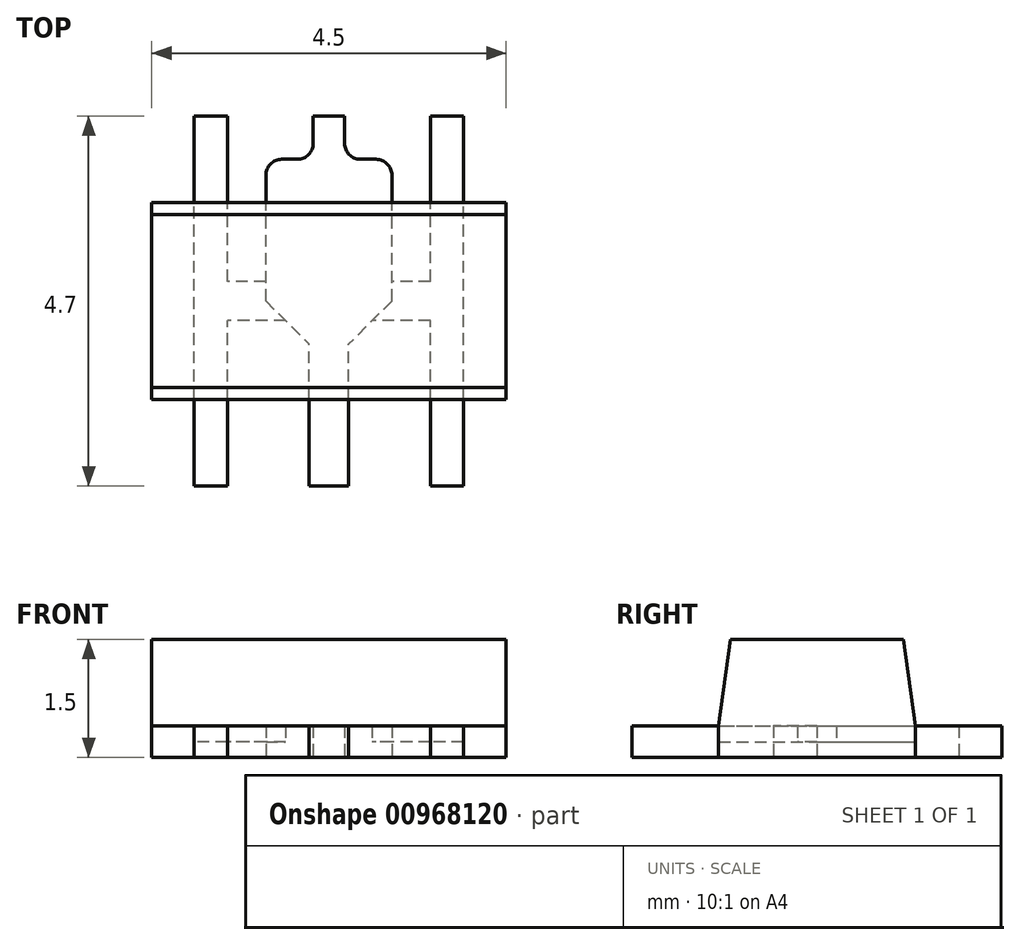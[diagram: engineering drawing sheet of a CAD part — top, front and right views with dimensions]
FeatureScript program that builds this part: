
annotation { "Feature Type Name" : "Feature", "Feature Type Description" : "" }
export const myFeature = defineFeature(function(context is Context, id is Id, definition is map)
    precondition{}
    {
        {
            assignVariable(context, id + "F0", {"name" : "A", "anyValue" : 1.5});
        }
        {
            assignVariable(context, id + "F1", {"name" : "E", "anyValue" : 2.5});
        }
        {
            assignVariable(context, id + "F2", {"name" : "E1", "anyValue" : 2.2});
        }
        {
            assignVariable(context, id + "F3", {"name" : "c", "anyValue" : 0.4});
        }
        {
            var Q0;
            Q0=qCreatedBy(makeId("Top.planeOp"),FACE);
            var sketch = newSketch(context, id + "F4", { "sketchPlane" : qUnion([Q0])});
            skLineSegment(sketch, "E0.bottom", {"start": v(2.25, -1.25) * mm, "end": v(-2.25, -1.25) * mm});
            skLineSegment(sketch, "E0.top", {"start": v(2.25, 1.25) * mm, "end": v(-2.25, 1.25) * mm});
            skLineSegment(sketch, "E0.left", {"start": v(2.25, -1.25) * mm, "end": v(2.25, 1.25) * mm});
            skLineSegment(sketch, "E0.right", {"start": v(-2.25, -1.25) * mm, "end": v(-2.25, 1.25) * mm});
            skPoint(sketch, "E0.middle", {"position": v(0, 0) * mm});
            skLineSegment(sketch, "E1.bottom", {"start": v(0.25, -2.35) * mm, "end": v(-0.25, -2.35) * mm});
            skLineSegment(sketch, "E1.left", {"start": v(0.25, -2.35) * mm, "end": v(0.25, -0.55) * mm});
            skLineSegment(sketch, "E1.right", {"start": v(-0.25, -2.35) * mm, "end": v(-0.25, -0.55) * mm});
            skPoint(sketch, "E1.middle", {"position": v(0, -1.17) * mm});
            skLineSegment(sketch, "E2.bottom", {"start": v(1.71, -2.35) * mm, "end": v(1.29, -2.35) * mm});
            skLineSegment(sketch, "E2.top", {"start": v(1.71, 2.35) * mm, "end": v(1.29, 2.35) * mm});
            skLineSegment(sketch, "E2.left", {"start": v(1.29, -2.35) * mm, "end": v(1.29, 2.35) * mm});
            skLineSegment(sketch, "E2.right", {"start": v(1.71, -2.35) * mm, "end": v(1.71, 2.35) * mm});
            skPoint(sketch, "E2.middle", {"position": v(1.5, 0) * mm});
            skLineSegment(sketch, "E3.top", {"start": v(0.2, 2.35) * mm, "end": v(-0.2, 2.35) * mm});
            skLineSegment(sketch, "E3.left", {"start": v(-0.2, 1.8) * mm, "end": v(-0.2, 2.35) * mm});
            skLineSegment(sketch, "E3.right", {"start": v(0.2, 1.8) * mm, "end": v(0.2, 2.35) * mm});
            skPoint(sketch, "E3.middle", {"position": v(0, 1.17) * mm});
            skLineSegment(sketch, "E4.bottom", {"start": v(-1.29, -2.35) * mm, "end": v(-1.7, -2.35) * mm});
            skLineSegment(sketch, "E4.top", {"start": v(-1.29, 2.35) * mm, "end": v(-1.7, 2.35) * mm});
            skLineSegment(sketch, "E4.left", {"start": v(-1.29, -2.35) * mm, "end": v(-1.29, 2.35) * mm});
            skLineSegment(sketch, "E4.right", {"start": v(-1.7, -2.35) * mm, "end": v(-1.7, 2.35) * mm});
            skPoint(sketch, "E4.middle", {"position": v(-1.5, 0) * mm});
            skLineSegment(sketch, "E5.top", {"start": v(0.8, 1.8) * mm, "end": v(0.2, 1.8) * mm});
            skLineSegment(sketch, "E5.left", {"start": v(0.8, 0) * mm, "end": v(0.8, 1.8) * mm});
            skLineSegment(sketch, "E5.right", {"start": v(-0.8, 0) * mm, "end": v(-0.8, 1.8) * mm});
            skPoint(sketch, "E5.middle", {"position": v(0, 0.9) * mm});
            skLineSegment(sketch, "E6", {"start": v(-1.29, -2.35) * mm, "end": v(-0.25, -2.35) * mm, "construction": true});
            skLineSegment(sketch, "E7", {"start": v(-0.2, 2.35) * mm, "end": v(0.2, 2.35) * mm, "construction": true});
            skLineSegment(sketch, "E8", {"start": v(-1.29, 2.35) * mm, "end": v(-0.2, 2.35) * mm, "construction": true});
            skLineSegment(sketch, "E9", {"start": v(0.2, 2.35) * mm, "end": v(1.29, 2.35) * mm, "construction": true});
            skLineSegment(sketch, "E10", {"start": v(0.25, -2.35) * mm, "end": v(1.29, -2.35) * mm, "construction": true});
            skPoint(sketch, "E11.orphan", {"position": v(-0.2, 0) * mm});
            skPoint(sketch, "E12.orphan", {"position": v(0.2, 0) * mm});
            skLineSegment(sketch, "E13.trimOffspring", {"start": v(-0.2, 1.8) * mm, "end": v(-0.8, 1.8) * mm});
            skLineSegment(sketch, "E14.bottom", {"start": v(1.71, -0.25) * mm, "end": v(-1.71, -0.25) * mm});
            skLineSegment(sketch, "E14.top", {"start": v(1.71, 0.25) * mm, "end": v(-1.71, 0.25) * mm});
            skLineSegment(sketch, "E14.left", {"start": v(1.71, -0.25) * mm, "end": v(1.71, 0.25) * mm});
            skLineSegment(sketch, "E14.right", {"start": v(-1.71, -0.25) * mm, "end": v(-1.71, 0.25) * mm});
            skLineSegment(sketch, "E15", {"start": v(-0.8, 0) * mm, "end": v(-0.25, -0.55) * mm});
            skLineSegment(sketch, "E16", {"start": v(0.8, 0) * mm, "end": v(0.25, -0.55) * mm});
            skPoint(sketch, "E17.orphan", {"position": v(-0.25, 0) * mm});
            skPoint(sketch, "E5.bottom.end.orphan", {"position": v(0.25, 0) * mm});
            skSolve(sketch);
        }
        {
            var Q0;
            {var subQ0=sQuery(id+"F4.wireOp",EDGE,"E5.left");var subQ1=sQuery(id+"F4.wireOp",EDGE,"E0.top");var subQ2=makeQuery(id+"F4.imprint","INTERSECT",VERTEX,{"derivedFrom":[subQ1,subQ0]});Q0=makeQuery(id+"F4.imprint","IMPRINT",FACE,{"disambiguationData":[TD([[makeQuery(id+"F4.imprint","IMPRINT",EDGE,{"disambiguationData":[TD([[subQ2,-1.0]])],"derivedFrom":subQ1}),1.0]])]});}
            var Q1;
            {var subQ0=sQuery(id+"F4.wireOp",EDGE,"E14.top");var subQ1=sQuery(id+"F4.wireOp",EDGE,"E4.left");var subQ2=makeQuery(id+"F4.imprint","INTERSECT",VERTEX,{"derivedFrom":[subQ1,subQ0]});Q1=makeQuery(id+"F4.imprint","IMPRINT",FACE,{"disambiguationData":[TD([[makeQuery(id+"F4.imprint","IMPRINT",EDGE,{"disambiguationData":[TD([[subQ2,1.0]])],"derivedFrom":subQ1}),-1.0]])]});}
            var Q2;
            {var subQ0=sQuery(id+"F4.wireOp",EDGE,"E14.top");var subQ5=sQuery(id+"F4.wireOp",EDGE,"E5.left");var subQ6=makeQuery(id+"F4.imprint","INTERSECT",VERTEX,{"derivedFrom":[subQ5,subQ0]});Q2=makeQuery(id+"F4.imprint","IMPRINT",FACE,{"disambiguationData":[TD([[makeQuery(id+"F4.imprint","IMPRINT",EDGE,{"disambiguationData":[TD([[subQ6,1.0]])],"derivedFrom":subQ5}),1.0]])]});}
            var Q3;
            {var subQ7=sQuery(id+"F4.wireOp",EDGE,"E0.bottom");var subQ9=sQuery(id+"F4.wireOp",EDGE,"E1.left");var subQ11=makeQuery(id+"F4.imprint","INTERSECT",VERTEX,{"derivedFrom":[subQ7,subQ9]});Q3=makeQuery(id+"F4.imprint","IMPRINT",FACE,{"disambiguationData":[TD([[makeQuery(id+"F4.imprint","IMPRINT",EDGE,{"disambiguationData":[TD([[subQ11,-1.0]])],"derivedFrom":subQ7}),-1.0]])]});}
            var Q4;
            {var subQ0=sQuery(id+"F4.wireOp",EDGE,"E14.top");var subQ1=sQuery(id+"F4.wireOp",EDGE,"E4.left");var subQ2=makeQuery(id+"F4.imprint","INTERSECT",VERTEX,{"derivedFrom":[subQ1,subQ0]});Q4=makeQuery(id+"F4.imprint","IMPRINT",FACE,{"disambiguationData":[TD([[makeQuery(id+"F4.imprint","IMPRINT",EDGE,{"disambiguationData":[TD([[subQ2,1.0]])],"derivedFrom":subQ1}),1.0]])]});}
            var Q5;
            {var subQ0=sQuery(id+"F4.wireOp",EDGE,"E4.right");var subQ1=sQuery(id+"F4.wireOp",EDGE,"E0.top");var subQ2=makeQuery(id+"F4.imprint","INTERSECT",VERTEX,{"derivedFrom":[subQ1,subQ0]});Q5=makeQuery(id+"F4.imprint","IMPRINT",FACE,{"disambiguationData":[TD([[makeQuery(id+"F4.imprint","IMPRINT",EDGE,{"disambiguationData":[TD([[subQ2,1.0]])],"derivedFrom":subQ1}),1.0]])]});}
            var Q6;
            {var subQ0=sQuery(id+"F4.wireOp",EDGE,"E4.left");var subQ1=sQuery(id+"F4.wireOp",EDGE,"E0.bottom");var subQ2=makeQuery(id+"F4.imprint","INTERSECT",VERTEX,{"derivedFrom":[subQ1,subQ0]});Q6=makeQuery(id+"F4.imprint","IMPRINT",FACE,{"disambiguationData":[TD([[makeQuery(id+"F4.imprint","IMPRINT",EDGE,{"disambiguationData":[TD([[subQ2,-1.0]])],"derivedFrom":subQ1}),-1.0]])]});}
            var Q7;
            {var subQ5=sQuery(id+"F4.wireOp",EDGE,"E4.bottom");Q7=makeQuery(id+"F4.imprint","IMPRINT",FACE,{"disambiguationData":[TD([[makeQuery(id+"F4.imprint","IMPRINT",EDGE,{"derivedFrom":subQ5}),-1.0]])]});}
            var Q8;
            {var subQ5=sQuery(id+"F4.wireOp",EDGE,"E1.bottom");Q8=makeQuery(id+"F4.imprint","IMPRINT",FACE,{"disambiguationData":[TD([[makeQuery(id+"F4.imprint","IMPRINT",EDGE,{"derivedFrom":subQ5}),-1.0]])]});}
            var Q9;
            {var subQ0=sQuery(id+"F4.wireOp",EDGE,"E14.top");var subQ5=sQuery(id+"F4.wireOp",EDGE,"E2.left");var subQ6=makeQuery(id+"F4.imprint","INTERSECT",VERTEX,{"derivedFrom":[subQ5,subQ0]});Q9=makeQuery(id+"F4.imprint","IMPRINT",FACE,{"disambiguationData":[TD([[makeQuery(id+"F4.imprint","IMPRINT",EDGE,{"disambiguationData":[TD([[subQ6,1.0]])],"derivedFrom":subQ5}),1.0]])]});}
            var Q10;
            {var subQ0=sQuery(id+"F4.wireOp",EDGE,"E2.left");var subQ1=sQuery(id+"F4.wireOp",EDGE,"E0.bottom");var subQ2=makeQuery(id+"F4.imprint","INTERSECT",VERTEX,{"derivedFrom":[subQ1,subQ0]});Q10=makeQuery(id+"F4.imprint","IMPRINT",FACE,{"disambiguationData":[TD([[makeQuery(id+"F4.imprint","IMPRINT",EDGE,{"disambiguationData":[TD([[subQ2,1.0]])],"derivedFrom":subQ1}),-1.0]])]});}
            var Q11;
            {var subQ5=sQuery(id+"F4.wireOp",EDGE,"E2.bottom");Q11=makeQuery(id+"F4.imprint","IMPRINT",FACE,{"disambiguationData":[TD([[makeQuery(id+"F4.imprint","IMPRINT",EDGE,{"derivedFrom":subQ5}),-1.0]])]});}
            var Q12;
            {var subQ0=sQuery(id+"F4.wireOp",EDGE,"E14.top");var subQ1=sQuery(id+"F4.wireOp",EDGE,"E2.left");var subQ2=makeQuery(id+"F4.imprint","INTERSECT",VERTEX,{"derivedFrom":[subQ1,subQ0]});Q12=makeQuery(id+"F4.imprint","IMPRINT",FACE,{"disambiguationData":[TD([[makeQuery(id+"F4.imprint","IMPRINT",EDGE,{"disambiguationData":[TD([[subQ2,1.0]])],"derivedFrom":subQ1}),-1.0]])]});}
            var Q13;
            {var subQ0=sQuery(id+"F4.wireOp",EDGE,"E2.left");var subQ1=sQuery(id+"F4.wireOp",EDGE,"E0.top");var subQ2=makeQuery(id+"F4.imprint","INTERSECT",VERTEX,{"derivedFrom":[subQ1,subQ0]});Q13=makeQuery(id+"F4.imprint","IMPRINT",FACE,{"disambiguationData":[TD([[makeQuery(id+"F4.imprint","IMPRINT",EDGE,{"disambiguationData":[TD([[subQ2,1.0]])],"derivedFrom":subQ1}),1.0]])]});}
            var Q14;
            {var subQ5=sQuery(id+"F4.wireOp",EDGE,"E2.top");Q14=makeQuery(id+"F4.imprint","IMPRINT",FACE,{"disambiguationData":[TD([[makeQuery(id+"F4.imprint","IMPRINT",EDGE,{"derivedFrom":subQ5}),1.0]])]});}
            var Q15;
            Q15=makeQuery(id+"F4.imprint","IMPRINT",FACE,{"disambiguationData":[TD([[makeQuery(id+"F4.imprint","IMPRINT",EDGE,{"derivedFrom":sQuery(id+"F4.wireOp",EDGE,"E3.top")}),1.0]])]});
            var Q16;
            {var subQ5=sQuery(id+"F4.wireOp",EDGE,"E4.top");Q16=makeQuery(id+"F4.imprint","IMPRINT",FACE,{"disambiguationData":[TD([[makeQuery(id+"F4.imprint","IMPRINT",EDGE,{"derivedFrom":subQ5}),1.0]])]});}
            extrude(context, id + "F5", {"entities" : qUnion([Q0, Q1, Q2, Q3, Q4, Q5, Q6, Q7, Q8, Q9, Q10, Q11, Q12, Q13, Q14, Q15, Q16]), "depth" : getVariable(context, 'c') * mm, "offsetDistance" : 25 * mm});
        }
        {
            var Q0;
            {var subQ0=sQuery(id+"F4.wireOp",EDGE,"E4.left");var subQ1=sQuery(id+"F4.wireOp",EDGE,"E0.bottom");var subQ2=makeQuery(id+"F4.imprint","INTERSECT",VERTEX,{"derivedFrom":[subQ1,subQ0]});Q0=makeQuery(id+"F4.imprint","IMPRINT",FACE,{"disambiguationData":[TD([[makeQuery(id+"F4.imprint","IMPRINT",EDGE,{"disambiguationData":[TD([[subQ2,-1.0]])],"derivedFrom":subQ1}),-1.0]])]});}
            var Q1;
            {var subQ0=sQuery(id+"F4.wireOp",EDGE,"E14.top");var subQ1=sQuery(id+"F4.wireOp",EDGE,"E4.left");var subQ2=makeQuery(id+"F4.imprint","INTERSECT",VERTEX,{"derivedFrom":[subQ1,subQ0]});Q1=makeQuery(id+"F4.imprint","IMPRINT",FACE,{"disambiguationData":[TD([[makeQuery(id+"F4.imprint","IMPRINT",EDGE,{"disambiguationData":[TD([[subQ2,1.0]])],"derivedFrom":subQ1}),1.0]])]});}
            var Q2;
            {var subQ0=sQuery(id+"F4.wireOp",EDGE,"E4.right");var subQ1=sQuery(id+"F4.wireOp",EDGE,"E0.top");var subQ2=makeQuery(id+"F4.imprint","INTERSECT",VERTEX,{"derivedFrom":[subQ1,subQ0]});Q2=makeQuery(id+"F4.imprint","IMPRINT",FACE,{"disambiguationData":[TD([[makeQuery(id+"F4.imprint","IMPRINT",EDGE,{"disambiguationData":[TD([[subQ2,1.0]])],"derivedFrom":subQ1}),1.0]])]});}
            var Q3;
            {var subQ0=sQuery(id+"F4.wireOp",EDGE,"E14.top");var subQ1=sQuery(id+"F4.wireOp",EDGE,"E4.left");var subQ2=makeQuery(id+"F4.imprint","INTERSECT",VERTEX,{"derivedFrom":[subQ1,subQ0]});Q3=makeQuery(id+"F4.imprint","IMPRINT",FACE,{"disambiguationData":[TD([[makeQuery(id+"F4.imprint","IMPRINT",EDGE,{"disambiguationData":[TD([[subQ2,1.0]])],"derivedFrom":subQ1}),-1.0]])]});}
            var Q4;
            {var subQ0=sQuery(id+"F4.wireOp",EDGE,"E14.top");var subQ5=sQuery(id+"F4.wireOp",EDGE,"E2.left");var subQ6=makeQuery(id+"F4.imprint","INTERSECT",VERTEX,{"derivedFrom":[subQ5,subQ0]});Q4=makeQuery(id+"F4.imprint","IMPRINT",FACE,{"disambiguationData":[TD([[makeQuery(id+"F4.imprint","IMPRINT",EDGE,{"disambiguationData":[TD([[subQ6,1.0]])],"derivedFrom":subQ5}),1.0]])]});}
            var Q5;
            {var subQ0=sQuery(id+"F4.wireOp",EDGE,"E2.left");var subQ1=sQuery(id+"F4.wireOp",EDGE,"E0.bottom");var subQ2=makeQuery(id+"F4.imprint","INTERSECT",VERTEX,{"derivedFrom":[subQ1,subQ0]});Q5=makeQuery(id+"F4.imprint","IMPRINT",FACE,{"disambiguationData":[TD([[makeQuery(id+"F4.imprint","IMPRINT",EDGE,{"disambiguationData":[TD([[subQ2,1.0]])],"derivedFrom":subQ1}),-1.0]])]});}
            var Q6;
            {var subQ0=sQuery(id+"F4.wireOp",EDGE,"E14.top");var subQ1=sQuery(id+"F4.wireOp",EDGE,"E2.left");var subQ2=makeQuery(id+"F4.imprint","INTERSECT",VERTEX,{"derivedFrom":[subQ1,subQ0]});Q6=makeQuery(id+"F4.imprint","IMPRINT",FACE,{"disambiguationData":[TD([[makeQuery(id+"F4.imprint","IMPRINT",EDGE,{"disambiguationData":[TD([[subQ2,1.0]])],"derivedFrom":subQ1}),-1.0]])]});}
            var Q7;
            {var subQ0=sQuery(id+"F4.wireOp",EDGE,"E2.left");var subQ1=sQuery(id+"F4.wireOp",EDGE,"E0.top");var subQ2=makeQuery(id+"F4.imprint","INTERSECT",VERTEX,{"derivedFrom":[subQ1,subQ0]});Q7=makeQuery(id+"F4.imprint","IMPRINT",FACE,{"disambiguationData":[TD([[makeQuery(id+"F4.imprint","IMPRINT",EDGE,{"disambiguationData":[TD([[subQ2,1.0]])],"derivedFrom":subQ1}),1.0]])]});}
            extrude(context, id + "F6", {"entities" : qUnion([Q0, Q1, Q2, Q3, Q4, Q5, Q6, Q7]), "operationType" : NewBodyOperationType.REMOVE, "depth" : (getVariable(context, 'c') / 2) * mm, "offsetDistance" : 25 * mm});
        }
        {
            var Q0;
            Q0=makeQuery(id+"F5.opExtrude","SWEPT_EDGE",EDGE,{"disambiguationData":[OSD([sQuery(id+"F4.wireOp",EDGE,"E5.right"),sQuery(id+"F4.wireOp",EDGE,"E13.trimOffspring")])]});
            var Q1;
            Q1=makeQuery(id+"F5.opExtrude","SWEPT_EDGE",EDGE,{"disambiguationData":[OSD([sQuery(id+"F4.wireOp",EDGE,"E3.left"),sQuery(id+"F4.wireOp",EDGE,"E13.trimOffspring")])]});
            var Q2;
            Q2=makeQuery(id+"F5.opExtrude","SWEPT_EDGE",EDGE,{"disambiguationData":[OSD([sQuery(id+"F4.wireOp",EDGE,"E3.right"),sQuery(id+"F4.wireOp",EDGE,"E5.top")])]});
            var Q3;
            Q3=makeQuery(id+"F5.opExtrude","SWEPT_EDGE",EDGE,{"disambiguationData":[OSD([sQuery(id+"F4.wireOp",EDGE,"E5.top"),sQuery(id+"F4.wireOp",EDGE,"E5.left")])]});
            fillet(context, id + "F7", {"entities" : qUnion([Q0, Q1, Q2, Q3]), "radius" : getVariable(context, 'c') / 2 * mm, "tangentPropagation" : true, "allowEdgeOverflow" : false});
        }
        {
            var Q0;
            {var subQ5=sQuery(id+"F4.wireOp",EDGE,"E1.right");var subQ7=sQuery(id+"F4.wireOp",EDGE,"E0.bottom");var subQ8=makeQuery(id+"F4.imprint","INTERSECT",VERTEX,{"derivedFrom":[subQ7,subQ5]});Q0=makeQuery(id+"F4.imprint","IMPRINT",FACE,{"disambiguationData":[TD([[makeQuery(id+"F4.imprint","IMPRINT",EDGE,{"disambiguationData":[TD([[subQ8,-1.0]])],"derivedFrom":subQ7}),-1.0]])]});}
            var Q1;
            {var subQ0=sQuery(id+"F4.wireOp",EDGE,"E4.left");var subQ1=sQuery(id+"F4.wireOp",EDGE,"E0.bottom");var subQ2=makeQuery(id+"F4.imprint","INTERSECT",VERTEX,{"derivedFrom":[subQ1,subQ0]});Q1=makeQuery(id+"F4.imprint","IMPRINT",FACE,{"disambiguationData":[TD([[makeQuery(id+"F4.imprint","IMPRINT",EDGE,{"disambiguationData":[TD([[subQ2,-1.0]])],"derivedFrom":subQ1}),-1.0]])]});}
            var Q2;
            {var subQ0=sQuery(id+"F4.wireOp",EDGE,"E14.top");var subQ1=sQuery(id+"F4.wireOp",EDGE,"E4.left");var subQ2=makeQuery(id+"F4.imprint","INTERSECT",VERTEX,{"derivedFrom":[subQ1,subQ0]});Q2=makeQuery(id+"F4.imprint","IMPRINT",FACE,{"disambiguationData":[TD([[makeQuery(id+"F4.imprint","IMPRINT",EDGE,{"disambiguationData":[TD([[subQ2,1.0]])],"derivedFrom":subQ1}),1.0]])]});}
            var Q3;
            {var subQ0=sQuery(id+"F4.wireOp",EDGE,"E4.right");var subQ1=sQuery(id+"F4.wireOp",EDGE,"E0.top");var subQ2=makeQuery(id+"F4.imprint","INTERSECT",VERTEX,{"derivedFrom":[subQ1,subQ0]});Q3=makeQuery(id+"F4.imprint","IMPRINT",FACE,{"disambiguationData":[TD([[makeQuery(id+"F4.imprint","IMPRINT",EDGE,{"disambiguationData":[TD([[subQ2,1.0]])],"derivedFrom":subQ1}),1.0]])]});}
            var Q4;
            {var subQ0=sQuery(id+"F4.wireOp",EDGE,"E5.right");var subQ1=sQuery(id+"F4.wireOp",EDGE,"E0.top");var subQ2=makeQuery(id+"F4.imprint","INTERSECT",VERTEX,{"derivedFrom":[subQ1,subQ0]});Q4=makeQuery(id+"F4.imprint","IMPRINT",FACE,{"disambiguationData":[TD([[makeQuery(id+"F4.imprint","IMPRINT",EDGE,{"disambiguationData":[TD([[subQ2,-1.0]])],"derivedFrom":subQ1}),1.0]])]});}
            var Q5;
            {var subQ0=sQuery(id+"F4.wireOp",EDGE,"E5.left");var subQ1=sQuery(id+"F4.wireOp",EDGE,"E0.top");var subQ2=makeQuery(id+"F4.imprint","INTERSECT",VERTEX,{"derivedFrom":[subQ1,subQ0]});Q5=makeQuery(id+"F4.imprint","IMPRINT",FACE,{"disambiguationData":[TD([[makeQuery(id+"F4.imprint","IMPRINT",EDGE,{"disambiguationData":[TD([[subQ2,-1.0]])],"derivedFrom":subQ1}),1.0]])]});}
            var Q6;
            {var subQ0=sQuery(id+"F4.wireOp",EDGE,"E14.top");var subQ1=sQuery(id+"F4.wireOp",EDGE,"E4.left");var subQ2=makeQuery(id+"F4.imprint","INTERSECT",VERTEX,{"derivedFrom":[subQ1,subQ0]});Q6=makeQuery(id+"F4.imprint","IMPRINT",FACE,{"disambiguationData":[TD([[makeQuery(id+"F4.imprint","IMPRINT",EDGE,{"disambiguationData":[TD([[subQ2,1.0]])],"derivedFrom":subQ1}),-1.0]])]});}
            var Q7;
            {var subQ7=sQuery(id+"F4.wireOp",EDGE,"E0.bottom");var subQ9=sQuery(id+"F4.wireOp",EDGE,"E1.left");var subQ11=makeQuery(id+"F4.imprint","INTERSECT",VERTEX,{"derivedFrom":[subQ7,subQ9]});Q7=makeQuery(id+"F4.imprint","IMPRINT",FACE,{"disambiguationData":[TD([[makeQuery(id+"F4.imprint","IMPRINT",EDGE,{"disambiguationData":[TD([[subQ11,-1.0]])],"derivedFrom":subQ7}),-1.0]])]});}
            var Q8;
            {var subQ0=sQuery(id+"F4.wireOp",EDGE,"E14.top");var subQ5=sQuery(id+"F4.wireOp",EDGE,"E5.left");var subQ6=makeQuery(id+"F4.imprint","INTERSECT",VERTEX,{"derivedFrom":[subQ5,subQ0]});Q8=makeQuery(id+"F4.imprint","IMPRINT",FACE,{"disambiguationData":[TD([[makeQuery(id+"F4.imprint","IMPRINT",EDGE,{"disambiguationData":[TD([[subQ6,1.0]])],"derivedFrom":subQ5}),1.0]])]});}
            var Q9;
            {var subQ3=sQuery(id+"F4.wireOp",EDGE,"E2.left");var subQ7=sQuery(id+"F4.wireOp",EDGE,"E0.bottom");var subQ9=makeQuery(id+"F4.imprint","INTERSECT",VERTEX,{"derivedFrom":[subQ7,subQ3]});Q9=makeQuery(id+"F4.imprint","IMPRINT",FACE,{"disambiguationData":[TD([[makeQuery(id+"F4.imprint","IMPRINT",EDGE,{"disambiguationData":[TD([[subQ9,-1.0]])],"derivedFrom":subQ7}),-1.0]])]});}
            var Q10;
            {var subQ0=sQuery(id+"F4.wireOp",EDGE,"E2.left");var subQ1=sQuery(id+"F4.wireOp",EDGE,"E0.bottom");var subQ2=makeQuery(id+"F4.imprint","INTERSECT",VERTEX,{"derivedFrom":[subQ1,subQ0]});Q10=makeQuery(id+"F4.imprint","IMPRINT",FACE,{"disambiguationData":[TD([[makeQuery(id+"F4.imprint","IMPRINT",EDGE,{"disambiguationData":[TD([[subQ2,1.0]])],"derivedFrom":subQ1}),-1.0]])]});}
            var Q11;
            {var subQ0=sQuery(id+"F4.wireOp",EDGE,"E14.top");var subQ5=sQuery(id+"F4.wireOp",EDGE,"E2.left");var subQ6=makeQuery(id+"F4.imprint","INTERSECT",VERTEX,{"derivedFrom":[subQ5,subQ0]});Q11=makeQuery(id+"F4.imprint","IMPRINT",FACE,{"disambiguationData":[TD([[makeQuery(id+"F4.imprint","IMPRINT",EDGE,{"disambiguationData":[TD([[subQ6,1.0]])],"derivedFrom":subQ5}),1.0]])]});}
            var Q12;
            {var subQ0=sQuery(id+"F4.wireOp",EDGE,"E14.top");var subQ1=sQuery(id+"F4.wireOp",EDGE,"E2.left");var subQ2=makeQuery(id+"F4.imprint","INTERSECT",VERTEX,{"derivedFrom":[subQ1,subQ0]});Q12=makeQuery(id+"F4.imprint","IMPRINT",FACE,{"disambiguationData":[TD([[makeQuery(id+"F4.imprint","IMPRINT",EDGE,{"disambiguationData":[TD([[subQ2,1.0]])],"derivedFrom":subQ1}),-1.0]])]});}
            var Q13;
            {var subQ4=sQuery(id+"F4.wireOp",EDGE,"E0.left");Q13=makeQuery(id+"F4.imprint","IMPRINT",FACE,{"disambiguationData":[TD([[makeQuery(id+"F4.imprint","IMPRINT",EDGE,{"derivedFrom":subQ4}),1.0]])]});}
            var Q14;
            {var subQ0=sQuery(id+"F4.wireOp",EDGE,"E5.left");var subQ1=sQuery(id+"F4.wireOp",EDGE,"E0.top");var subQ2=makeQuery(id+"F4.imprint","INTERSECT",VERTEX,{"derivedFrom":[subQ1,subQ0]});Q14=makeQuery(id+"F4.imprint","IMPRINT",FACE,{"disambiguationData":[TD([[makeQuery(id+"F4.imprint","IMPRINT",EDGE,{"disambiguationData":[TD([[subQ2,1.0]])],"derivedFrom":subQ1}),1.0]])]});}
            var Q15;
            {var subQ0=sQuery(id+"F4.wireOp",EDGE,"E2.left");var subQ1=sQuery(id+"F4.wireOp",EDGE,"E0.top");var subQ2=makeQuery(id+"F4.imprint","INTERSECT",VERTEX,{"derivedFrom":[subQ1,subQ0]});Q15=makeQuery(id+"F4.imprint","IMPRINT",FACE,{"disambiguationData":[TD([[makeQuery(id+"F4.imprint","IMPRINT",EDGE,{"disambiguationData":[TD([[subQ2,1.0]])],"derivedFrom":subQ1}),1.0]])]});}
            var Q16;
            {var subQ4=sQuery(id+"F4.wireOp",EDGE,"E0.right");Q16=makeQuery(id+"F4.imprint","IMPRINT",FACE,{"disambiguationData":[TD([[makeQuery(id+"F4.imprint","IMPRINT",EDGE,{"derivedFrom":subQ4}),-1.0]])]});}
            extrude(context, id + "F8", {"entities" : qUnion([Q0, Q1, Q2, Q3, Q4, Q5, Q6, Q7, Q8, Q9, Q10, Q11, Q12, Q13, Q14, Q15, Q16]), "depth" : (getVariable(context, 'A')) * mm, "offsetDistance" : 25 * mm});
        }
        {
            var Q0;
            Q0=makeQuery(id+"F8.opExtrude","CAP_EDGE",EDGE,{"disambiguationData":[OSD([sQuery(id+"F4.wireOp",EDGE,"E0.bottom")])],"isStart":false});
            var Q1;
            Q1=makeQuery(id+"F8.opExtrude","CAP_EDGE",EDGE,{"disambiguationData":[OSD([sQuery(id+"F4.wireOp",EDGE,"E0.top")])],"isStart":false});
            chamfer(context, id + "F9", {"entities" : qUnion([Q0, Q1]), "chamferType" : ChamferType.TWO_OFFSETS, "width1" : (getVariable(context, 'A') - getVariable(context, 'c')) * mm, "oppositeDirection" : false, "width2" : (getVariable(context, 'E') - getVariable(context, 'E1')) / 2 * mm, "tangentPropagation" : true});
        }
        {
            var Q0;
            {var subQ0=sQuery(id+"F4.wireOp",EDGE,"E14.top");var subQ5=sQuery(id+"F4.wireOp",EDGE,"E5.left");var subQ6=makeQuery(id+"F4.imprint","INTERSECT",VERTEX,{"derivedFrom":[subQ5,subQ0]});Q0=makeQuery(id+"F4.imprint","IMPRINT",FACE,{"disambiguationData":[TD([[makeQuery(id+"F4.imprint","IMPRINT",EDGE,{"disambiguationData":[TD([[subQ6,1.0]])],"derivedFrom":subQ5}),1.0]])]});}
            var Q1;
            {var subQ7=sQuery(id+"F4.wireOp",EDGE,"E0.bottom");var subQ9=sQuery(id+"F4.wireOp",EDGE,"E1.left");var subQ11=makeQuery(id+"F4.imprint","INTERSECT",VERTEX,{"derivedFrom":[subQ7,subQ9]});Q1=makeQuery(id+"F4.imprint","IMPRINT",FACE,{"disambiguationData":[TD([[makeQuery(id+"F4.imprint","IMPRINT",EDGE,{"disambiguationData":[TD([[subQ11,-1.0]])],"derivedFrom":subQ7}),-1.0]])]});}
            var Q2;
            {var subQ0=sQuery(id+"F4.wireOp",EDGE,"E5.left");var subQ1=sQuery(id+"F4.wireOp",EDGE,"E0.top");var subQ2=makeQuery(id+"F4.imprint","INTERSECT",VERTEX,{"derivedFrom":[subQ1,subQ0]});Q2=makeQuery(id+"F4.imprint","IMPRINT",FACE,{"disambiguationData":[TD([[makeQuery(id+"F4.imprint","IMPRINT",EDGE,{"disambiguationData":[TD([[subQ2,-1.0]])],"derivedFrom":subQ1}),1.0]])]});}
            extrude(context, id + "F10", {"entities" : qUnion([Q0, Q1, Q2]), "operationType" : NewBodyOperationType.REMOVE, "depth" : getVariable(context, 'c') * mm, "offsetDistance" : 25 * mm});
        }
        {
            var Q0;
            {var subQ0=sQuery(id+"F4.wireOp",EDGE,"E5.right");var subQ1=sQuery(id+"F4.wireOp",EDGE,"E5.left");var subQ2=sQuery(id+"F4.wireOp",EDGE,"E5.top");var subQ3=sQuery(id+"F4.wireOp",EDGE,"E3.right");var subQ4=sQuery(id+"F4.wireOp",EDGE,"E3.left");var subQ5=sQuery(id+"F4.wireOp",EDGE,"E1.bottom");var subQ6=sQuery(id+"F4.wireOp",EDGE,"E13.trimOffspring");var subQ7=sQuery(id+"F4.wireOp",EDGE,"E3.top");var subQ8=sQuery(id+"F4.wireOp",EDGE,"E1.left");var subQ9=sQuery(id+"F4.wireOp",EDGE,"E15");var subQ10=sQuery(id+"F4.wireOp",EDGE,"E1.right");var subQ11=sQuery(id+"F4.wireOp",EDGE,"E16");Q0=makeQuery(id+"F6.boolean.opBoolean","SPLIT",FACE,{"disambiguationData":[TD([makeQuery(id+"F5.opExtrude","SWEPT_FACE",FACE,{"disambiguationData":[OSD([subQ5])]})])],"derivedFrom":makeQuery(id+"F5.opExtrude","CAP_FACE",FACE,{"disambiguationData":[OSD([subQ5,subQ8,subQ10,sQuery(id+"F4.wireOp",EDGE,"E2.bottom"),sQuery(id+"F4.wireOp",EDGE,"E2.top"),sQuery(id+"F4.wireOp",EDGE,"E2.left"),sQuery(id+"F4.wireOp",EDGE,"E2.right"),subQ7,subQ4,subQ3,sQuery(id+"F4.wireOp",EDGE,"E4.bottom"),sQuery(id+"F4.wireOp",EDGE,"E4.top"),sQuery(id+"F4.wireOp",EDGE,"E4.left"),sQuery(id+"F4.wireOp",EDGE,"E4.right"),subQ2,subQ1,subQ0,subQ6,sQuery(id+"F4.wireOp",EDGE,"E14.bottom"),sQuery(id+"F4.wireOp",EDGE,"E14.top"),subQ9,subQ11])],"isStart":true})});}
            var sketch = newSketch(context, id + "F11", { "sketchPlane" : qUnion([Q0])});
            skLineSegment(sketch, "E18.bottom", {"start": v(1.85, -2.6) * mm, "end": v(-1.85, -2.6) * mm, "construction": true});
            skLineSegment(sketch, "E18.top", {"start": v(1.85, 2.6) * mm, "end": v(-1.85, 2.6) * mm, "construction": true});
            skLineSegment(sketch, "E18.left", {"start": v(1.85, -2.6) * mm, "end": v(1.85, 2.6) * mm, "construction": true});
            skLineSegment(sketch, "E18.right", {"start": v(-1.85, -2.6) * mm, "end": v(-1.85, 2.6) * mm, "construction": true});
            skPoint(sketch, "E18.middle", {"position": v(0, 0) * mm});
            skLineSegment(sketch, "E19.bottom", {"start": v(0.5, -2.6) * mm, "end": v(-0.5, -2.6) * mm});
            skLineSegment(sketch, "E19.top", {"start": v(0.5, 2.6) * mm, "end": v(-0.5, 2.6) * mm});
            skLineSegment(sketch, "E19.left", {"start": v(0.5, -2.6) * mm, "end": v(0.5, -0.9) * mm});
            skLineSegment(sketch, "E19.right", {"start": v(-0.5, -2.6) * mm, "end": v(-0.5, -0.9) * mm});
            skLineSegment(sketch, "E20.bottom", {"start": v(-1.15, -2.6) * mm, "end": v(-1.85, -2.6) * mm});
            skLineSegment(sketch, "E20.top", {"start": v(-1.15, -1.1) * mm, "end": v(-1.85, -1.1) * mm});
            skLineSegment(sketch, "E20.left", {"start": v(-1.15, -2.6) * mm, "end": v(-1.15, -1.1) * mm});
            skLineSegment(sketch, "E20.right", {"start": v(-1.85, -2.6) * mm, "end": v(-1.85, -1.1) * mm});
            skPoint(sketch, "E20.middle", {"position": v(-1.5, -1.85) * mm});
            skLineSegment(sketch, "E21.bottom", {"start": v(1.85, -2.6) * mm, "end": v(1.15, -2.6) * mm});
            skLineSegment(sketch, "E21.top", {"start": v(1.85, -1.1) * mm, "end": v(1.15, -1.1) * mm});
            skLineSegment(sketch, "E21.left", {"start": v(1.85, -2.6) * mm, "end": v(1.85, -1.1) * mm});
            skLineSegment(sketch, "E21.right", {"start": v(1.15, -2.6) * mm, "end": v(1.15, -1.1) * mm});
            skPoint(sketch, "E21.middle", {"position": v(1.5, -1.85) * mm});
            skLineSegment(sketch, "E22.bottom", {"start": v(-1.15, 1.1) * mm, "end": v(-1.85, 1.1) * mm});
            skLineSegment(sketch, "E22.top", {"start": v(-1.15, 2.6) * mm, "end": v(-1.85, 2.6) * mm});
            skLineSegment(sketch, "E22.left", {"start": v(-1.15, 1.1) * mm, "end": v(-1.15, 2.6) * mm});
            skLineSegment(sketch, "E22.right", {"start": v(-1.85, 1.1) * mm, "end": v(-1.85, 2.6) * mm});
            skPoint(sketch, "E22.middle", {"position": v(-1.5, 1.85) * mm});
            skLineSegment(sketch, "E23.bottom", {"start": v(1.85, 1.1) * mm, "end": v(1.15, 1.1) * mm});
            skLineSegment(sketch, "E23.top", {"start": v(1.85, 2.6) * mm, "end": v(1.15, 2.6) * mm});
            skLineSegment(sketch, "E23.left", {"start": v(1.85, 1.1) * mm, "end": v(1.85, 2.6) * mm});
            skLineSegment(sketch, "E23.right", {"start": v(1.15, 1.1) * mm, "end": v(1.15, 2.6) * mm});
            skPoint(sketch, "E23.middle", {"position": v(1.5, 1.85) * mm});
            skLineSegment(sketch, "E24.left", {"start": v(1, -0.4) * mm, "end": v(1, 0.4) * mm});
            skLineSegment(sketch, "E24.right", {"start": v(-1, -0.4) * mm, "end": v(-1, 0.4) * mm});
            skLineSegment(sketch, "E25", {"start": v(-1, 0.4) * mm, "end": v(-0.5, 0.9) * mm});
            skLineSegment(sketch, "E26", {"start": v(1, 0.4) * mm, "end": v(0.5, 0.9) * mm});
            skLineSegment(sketch, "E27", {"start": v(1, -0.4) * mm, "end": v(0.5, -0.9) * mm});
            skLineSegment(sketch, "E28", {"start": v(-1, -0.4) * mm, "end": v(-0.5, -0.9) * mm});
            skLineSegment(sketch, "E29.trimOffspring", {"start": v(0.5, 0.9) * mm, "end": v(0.5, 2.6) * mm});
            skLineSegment(sketch, "E30.trimOffspring", {"start": v(-0.5, 0.9) * mm, "end": v(-0.5, 2.6) * mm});
            skLineSegment(sketch, "E31.bottom", {"start": v(2.25, 1.25) * mm, "end": v(-2.25, 1.25) * mm, "construction": true});
            skLineSegment(sketch, "E31.top", {"start": v(2.25, -1.25) * mm, "end": v(-2.25, -1.25) * mm, "construction": true});
            skLineSegment(sketch, "E31.left", {"start": v(2.25, 1.25) * mm, "end": v(2.25, -1.25) * mm, "construction": true});
            skLineSegment(sketch, "E31.right", {"start": v(-2.25, 1.25) * mm, "end": v(-2.25, -1.25) * mm, "construction": true});
            skSolve(sketch);
        }
    });
